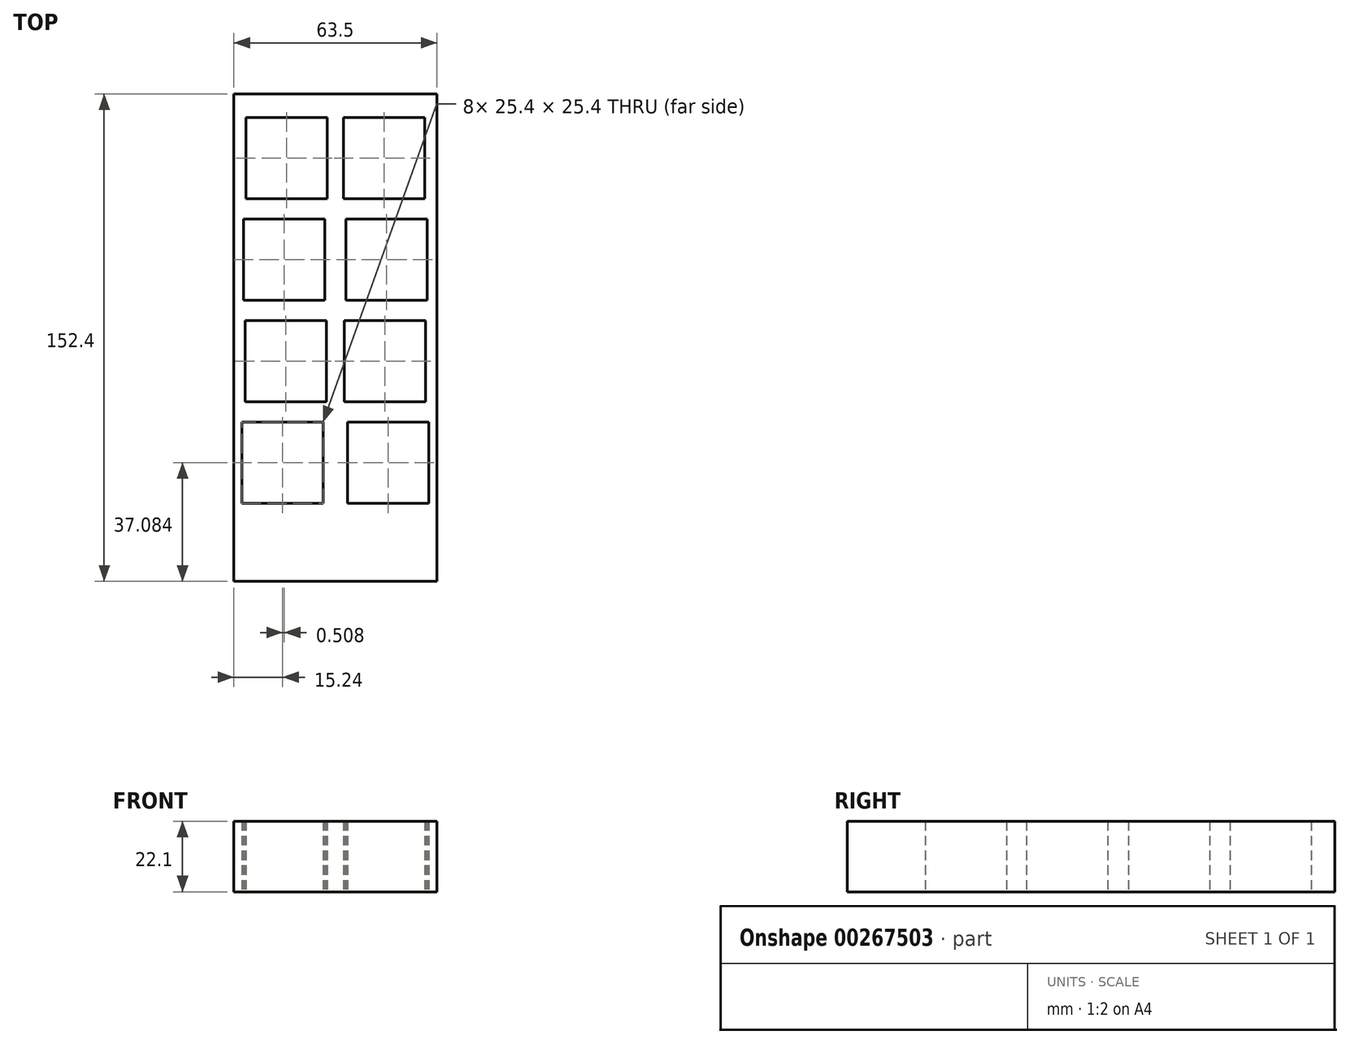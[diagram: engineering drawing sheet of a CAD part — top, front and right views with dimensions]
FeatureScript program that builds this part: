
annotation { "Feature Type Name" : "Feature", "Feature Type Description" : "" }
export const myFeature = defineFeature(function(context is Context, id is Id, definition is map)
    precondition{}
    {
        {
            var Q0;
            Q0=qCreatedBy(makeId("Top.planeOp"),FACE);
            var sketch = newSketch(context, id + "F0", { "sketchPlane" : qUnion([Q0])});
            skLineSegment(sketch, "E0.bottom", {"start": v(31.75, 76.2) * mm, "end": v(-31.75, 76.2) * mm});
            skLineSegment(sketch, "E0.top", {"start": v(31.75, -76.2) * mm, "end": v(-31.75, -76.2) * mm});
            skLineSegment(sketch, "E0.left", {"start": v(31.75, 76.2) * mm, "end": v(31.75, -76.2) * mm});
            skLineSegment(sketch, "E0.right", {"start": v(-31.75, 76.2) * mm, "end": v(-31.75, -76.2) * mm});
            skPoint(sketch, "E0.middle", {"position": v(0, 0) * mm});
            skLineSegment(sketch, "E1.bottom", {"start": v(-2.57, 68.86) * mm, "end": v(-27.97, 68.86) * mm});
            skLineSegment(sketch, "E1.top", {"start": v(-2.57, 43.46) * mm, "end": v(-27.97, 43.46) * mm});
            skLineSegment(sketch, "E1.left", {"start": v(-2.57, 68.86) * mm, "end": v(-2.57, 43.46) * mm});
            skLineSegment(sketch, "E1.right", {"start": v(-27.97, 68.86) * mm, "end": v(-27.97, 43.46) * mm});
            skPoint(sketch, "E1.middle", {"position": v(-15.27, 56.16) * mm});
            skPoint(sketch, "E2.1.0.0", {"position": v(16.48, 56.16) * mm});
            skPoint(sketch, "E2.2.0.0", {"position": v(48.23, 56.16) * mm});
            skLineSegment(sketch, "E2.direction1", {"start": v(-15.27, 56.16) * mm, "end": v(16.48, 56.16) * mm, "construction": true});
            skPoint(sketch, "E3.1.0.0", {"position": v(16, 24.38) * mm});
            skPoint(sketch, "E3.2.0.0", {"position": v(15.52, -7.4) * mm});
            skLineSegment(sketch, "E3.direction1", {"start": v(16.48, 56.16) * mm, "end": v(16, 24.38) * mm, "construction": true});
            skPoint(sketch, "E4.1.0.0", {"position": v(16.26, -7.37) * mm});
            skPoint(sketch, "E4.2.0.0", {"position": v(16.51, -39.12) * mm});
            skLineSegment(sketch, "E4.direction1", {"start": v(16, 24.38) * mm, "end": v(16.26, -7.37) * mm, "construction": true});
            skPoint(sketch, "E5.2.0.0", {"position": v(16.76, -70.87) * mm});
            skLineSegment(sketch, "E5.direction1", {"start": v(16.26, -7.37) * mm, "end": v(16.51, -39.12) * mm, "construction": true});
            skPoint(sketch, "E6.MirrorP", {"position": v(-16.48, 56.16) * mm});
            skPoint(sketch, "E7.MirrorP", {"position": v(-16, 24.38) * mm});
            skPoint(sketch, "E8.MirrorP", {"position": v(-15.52, -7.4) * mm});
            skLineSegment(sketch, "E9.MirrorCS", {"start": v(-16.26, -7.37) * mm, "end": v(-16.51, -39.12) * mm, "construction": true});
            skLineSegment(sketch, "E10.MirrorCS", {"start": v(-16, 24.38) * mm, "end": v(-16.26, -7.37) * mm, "construction": true});
            skLineSegment(sketch, "E11.MirrorCS", {"start": v(-16.48, 56.16) * mm, "end": v(-16, 24.38) * mm, "construction": true});
            skLineSegment(sketch, "E12.MirrorCS", {"start": v(2.57, 68.86) * mm, "end": v(2.57, 43.46) * mm});
            skLineSegment(sketch, "E13.MirrorCS", {"start": v(2.57, 43.46) * mm, "end": v(27.97, 43.46) * mm});
            skLineSegment(sketch, "E14.MirrorCS", {"start": v(2.57, 68.86) * mm, "end": v(27.97, 68.86) * mm});
            skLineSegment(sketch, "E15.MirrorCS", {"start": v(27.97, 68.86) * mm, "end": v(27.97, 43.46) * mm});
            skLineSegment(sketch, "E16.bottom", {"start": v(-3.3, 37.08) * mm, "end": v(-28.7, 37.08) * mm});
            skLineSegment(sketch, "E16.top", {"start": v(-3.3, 11.68) * mm, "end": v(-28.7, 11.68) * mm});
            skLineSegment(sketch, "E16.left", {"start": v(-3.3, 37.08) * mm, "end": v(-3.3, 11.68) * mm});
            skLineSegment(sketch, "E16.right", {"start": v(-28.7, 37.08) * mm, "end": v(-28.7, 11.68) * mm});
            skLineSegment(sketch, "E17.bottom", {"start": v(-2.82, 5.3) * mm, "end": v(-28.22, 5.3) * mm});
            skLineSegment(sketch, "E17.top", {"start": v(-2.82, -20.1) * mm, "end": v(-28.22, -20.1) * mm});
            skLineSegment(sketch, "E17.left", {"start": v(-2.82, 5.3) * mm, "end": v(-2.82, -20.1) * mm});
            skLineSegment(sketch, "E17.right", {"start": v(-28.22, 5.3) * mm, "end": v(-28.22, -20.1) * mm});
            skLineSegment(sketch, "E18.bottom", {"start": v(-3.8, -26.42) * mm, "end": v(-29.2, -26.42) * mm});
            skLineSegment(sketch, "E18.top", {"start": v(-3.8, -51.82) * mm, "end": v(-29.21, -51.82) * mm});
            skLineSegment(sketch, "E18.left", {"start": v(-3.8, -26.42) * mm, "end": v(-3.8, -51.82) * mm});
            skLineSegment(sketch, "E18.right", {"start": v(-29.2, -26.42) * mm, "end": v(-29.2, -51.82) * mm});
            skPoint(sketch, "E18.middle", {"position": v(-16.51, -39.12) * mm});
            skLineSegment(sketch, "E19.MirrorCS", {"start": v(3.3, 37.08) * mm, "end": v(28.7, 37.08) * mm});
            skLineSegment(sketch, "E20.MirrorCS", {"start": v(28.7, 37.08) * mm, "end": v(28.7, 11.68) * mm});
            skLineSegment(sketch, "E21.MirrorCS", {"start": v(3.3, 11.68) * mm, "end": v(28.7, 11.68) * mm});
            skLineSegment(sketch, "E22.MirrorCS", {"start": v(3.3, 37.08) * mm, "end": v(3.3, 11.68) * mm});
            skLineSegment(sketch, "E23.MirrorCS", {"start": v(2.82, 5.3) * mm, "end": v(2.82, -20.1) * mm});
            skLineSegment(sketch, "E24.MirrorCS", {"start": v(2.82, 5.3) * mm, "end": v(28.22, 5.3) * mm});
            skLineSegment(sketch, "E25.MirrorCS", {"start": v(28.22, 5.3) * mm, "end": v(28.22, -20.1) * mm});
            skLineSegment(sketch, "E26.MirrorCS", {"start": v(2.82, -20.1) * mm, "end": v(28.22, -20.1) * mm});
            skLineSegment(sketch, "E27.MirrorCS", {"start": v(3.8, -26.42) * mm, "end": v(29.2, -26.42) * mm});
            skLineSegment(sketch, "E28.MirrorCS", {"start": v(3.8, -26.42) * mm, "end": v(3.8, -51.82) * mm});
            skLineSegment(sketch, "E29.MirrorCS", {"start": v(29.2, -26.42) * mm, "end": v(29.2, -51.82) * mm});
            skLineSegment(sketch, "E30.MirrorCS", {"start": v(3.8, -51.82) * mm, "end": v(29.21, -51.82) * mm});
            skSolve(sketch);
        }
        {
            var Q0;
            Q0=makeQuery(id+"F0.imprint","IMPRINT",FACE,{"disambiguationData":[TD([[makeQuery(id+"F0.imprint","IMPRINT",EDGE,{"derivedFrom":sQuery(id+"F0.wireOp",EDGE,"E0.bottom")}),1.0]])]});
            extrude(context, id + "F1", {"entities" : qUnion([Q0]), "depth" : 22.1 * mm});
        }
    });
